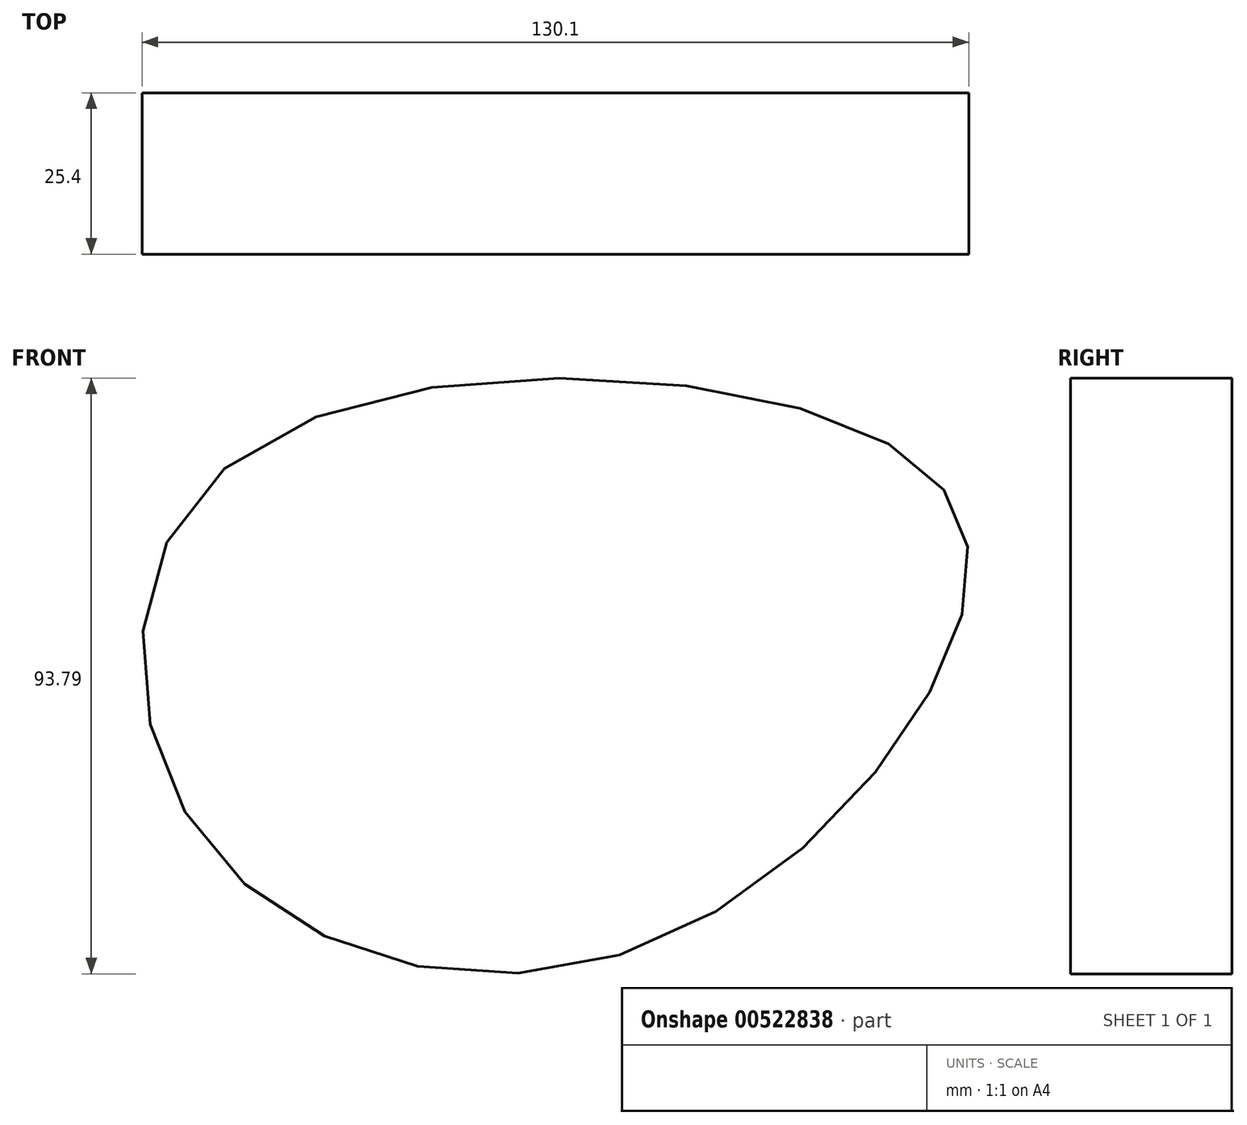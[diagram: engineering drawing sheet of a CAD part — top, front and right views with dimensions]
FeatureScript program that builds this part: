
annotation { "Feature Type Name" : "Feature", "Feature Type Description" : "" }
export const myFeature = defineFeature(function(context is Context, id is Id, definition is map)
    precondition{}
    {
        {
            var Q0;
            Q0=qCreatedBy(makeId("Front.planeOp"),FACE);
            var sketch = newSketch(context, id + "F0", { "sketchPlane" : qUnion([Q0])});
            skFitSpline(sketch, "E0", {"points": [v(-48.22, 58.62) * mm, v(53.34, 64.04) * mm, v(68, 36.22) * mm, v(15.9, -17.37) * mm, v(-51.37, 0) * mm, v(-48.22, 58.62) * mm]});
            skSolve(sketch);
        }
        {
            var Q0;
            Q0 = qSketchRegion(id + "F0", true);
            extrude(context, id + "F1", {"entities" : qUnion([Q0]), "depth" : 25.4 * mm, "offsetDistance" : 25.4 * mm});
        }
    });
